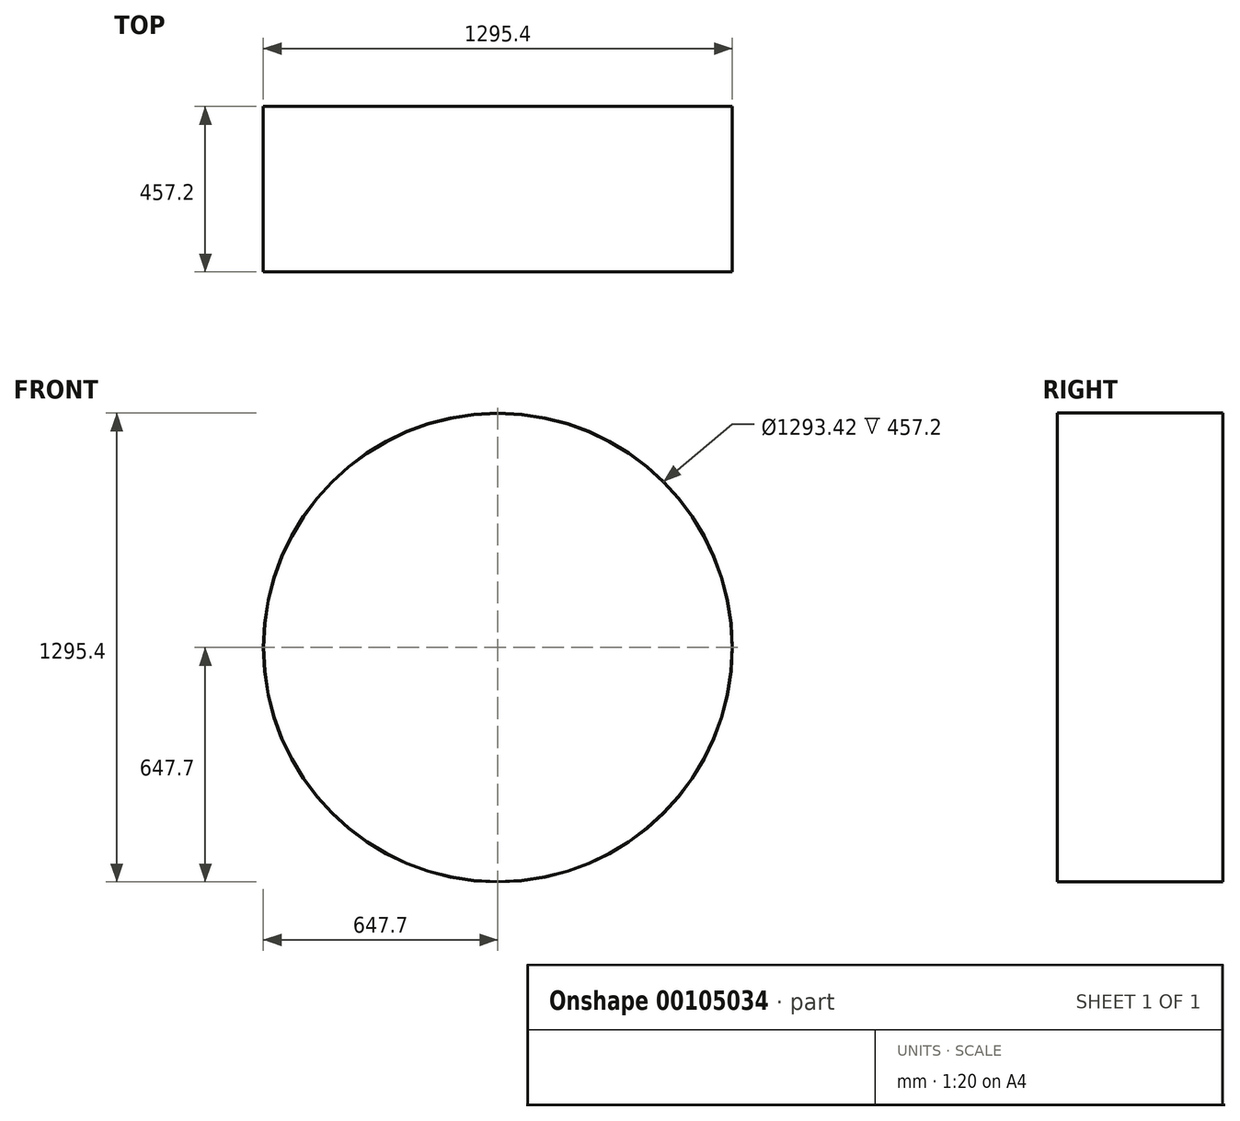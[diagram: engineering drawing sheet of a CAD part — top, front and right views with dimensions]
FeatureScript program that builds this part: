
annotation { "Feature Type Name" : "Feature", "Feature Type Description" : "" }
export const myFeature = defineFeature(function(context is Context, id is Id, definition is map)
    precondition{}
    {
        {
            var Q0;
            Q0=qCreatedBy(makeId("Front.planeOp"),FACE);
            var sketch = newSketch(context, id + "F0", { "sketchPlane" : qUnion([Q0])});
            skCircle(sketch, "E0", {"center": v(0, 0) * mm, "radius": 647.7 * mm});
            skCircle(sketch, "E1", {"center": v(0, 0) * mm, "radius": 646.7 * mm});
            skSolve(sketch);
        }
        {
            var Q0;
            Q0 = qSketchRegion(id + "F0", true);
            extrude(context, id + "F1", {"entities" : qUnion([Q0]), "depth" : 457.2 * mm});
        }
    });
